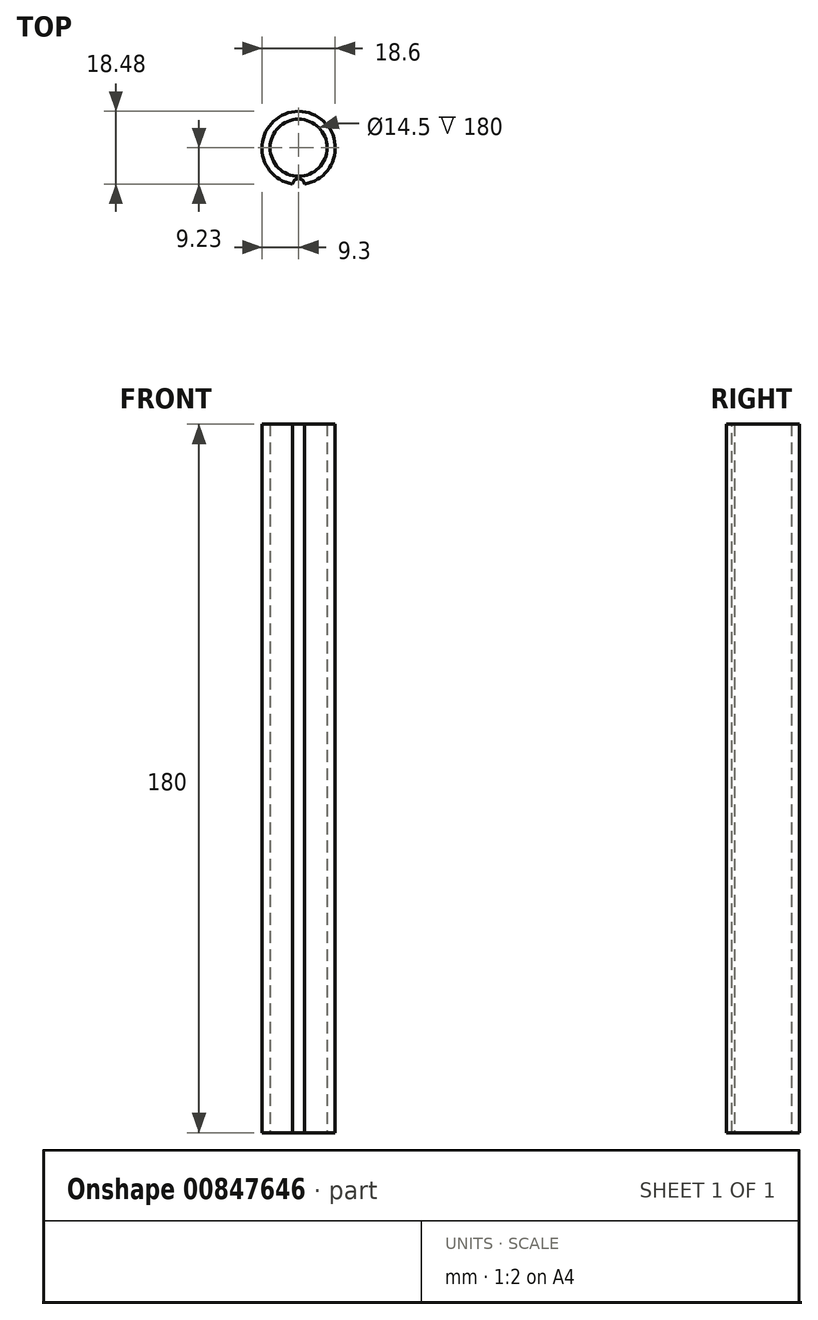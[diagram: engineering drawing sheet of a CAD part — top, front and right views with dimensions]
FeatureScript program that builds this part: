
annotation { "Feature Type Name" : "Feature", "Feature Type Description" : "" }
export const myFeature = defineFeature(function(context is Context, id is Id, definition is map)
    precondition{}
    {
        {
            var Q0;
            Q0=qCreatedBy(makeId("Top.planeOp"),FACE);
            var sketch = newSketch(context, id + "F0", { "sketchPlane" : qUnion([Q0])});
            skCircle(sketch, "E0", {"center": v(0, -0.05) * mm, "radius": 9.3 * mm});
            skCircle(sketch, "E1", {"center": v(0, 0) * mm, "radius": 7.25 * mm});
            skSolve(sketch);
        }
        {
            var Q0;
            Q0=makeQuery(id+"F0.imprint","IMPRINT",FACE,{"disambiguationData":[TD([[makeQuery(id+"F0.imprint","IMPRINT",EDGE,{"derivedFrom":sQuery(id+"F0.wireOp",EDGE,"E0")}),1.0]])]});
            extrude(context, id + "F1", {"entities" : qUnion([Q0]), "depth" : 180 * mm, "offsetDistance" : 25 * mm});
        }
        {
            var Q0;
            Q0=makeQuery(id+"F1.opExtrude","CAP_FACE",FACE,{"disambiguationData":[OSD([sQuery(id+"F0.wireOp",EDGE,"E0"),sQuery(id+"F0.wireOp",EDGE,"E1")])],"isStart":false});
            var sketch = newSketch(context, id + "F2", { "sketchPlane" : qUnion([Q0])});
            skCircle(sketch, "E2", {"center": v(0, -9.35) * mm, "radius": 1.5 * mm});
            skSolve(sketch);
        }
        {
            var Q0;
            {var subQ0=sQuery(id+"F2.wireOp",EDGE,"E2");var subQ1=makeQuery(id+"F1.opExtrude","CAP_EDGE",EDGE,{"disambiguationData":[OSD([sQuery(id+"F0.wireOp",EDGE,"E0")])],"isStart":false});var subQ2=makeQuery(id+"F2.imprint","INTERSECT",VERTEX,{"disambiguationData":[OD(0.0)],"derivedFrom":[subQ1,subQ0]});Q0=makeQuery(id+"F2.imprint","IMPRINT",FACE,{"disambiguationData":[TD([[makeQuery(id+"F2.imprint","IMPRINT",EDGE,{"disambiguationData":[TD([[subQ2,1.0]])],"derivedFrom":subQ0}),1.0]])]});}
            extrude(context, id + "F3", {"entities" : qUnion([Q0]), "operationType" : NewBodyOperationType.REMOVE, "endBound" : BoundingType.THROUGH_ALL, "oppositeDirection" : true, "depth" : 25 * mm, "offsetDistance" : 25 * mm});
        }
    });
